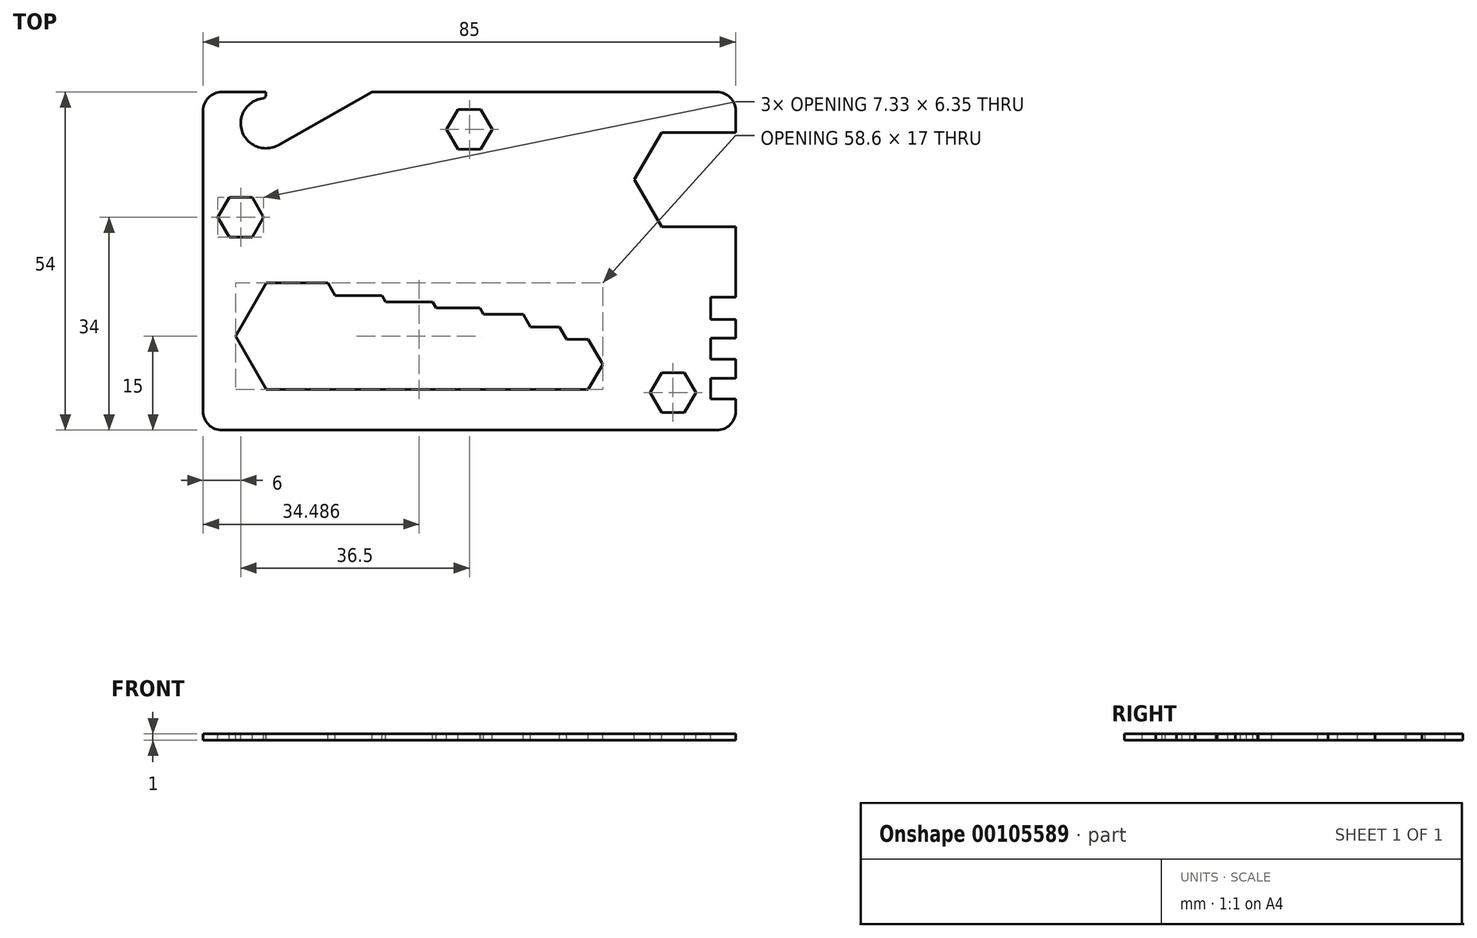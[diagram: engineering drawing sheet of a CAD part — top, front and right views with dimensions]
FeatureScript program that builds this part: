
annotation { "Feature Type Name" : "Feature", "Feature Type Description" : "" }
export const myFeature = defineFeature(function(context is Context, id is Id, definition is map)
    precondition{}
    {
        {
            var Q0;
            Q0=qCreatedBy(makeId("Top.planeOp"),FACE);
            var sketch = newSketch(context, id + "F0", { "sketchPlane" : qUnion([Q0])});
            skLineSegment(sketch, "E0.bottom", {"start": v(-42.5, 27) * mm, "end": v(42.5, 27) * mm});
            skLineSegment(sketch, "E0.top", {"start": v(-42.5, -27) * mm, "end": v(42.5, -27) * mm});
            skLineSegment(sketch, "E0.left", {"start": v(-42.5, 27) * mm, "end": v(-42.5, -27) * mm});
            skLineSegment(sketch, "E0.right", {"start": v(42.5, 27) * mm, "end": v(42.5, -27) * mm});
            skPoint(sketch, "E0.middle", {"position": v(0, 0) * mm});
            skSolve(sketch);
        }
        {
            var Q0;
            Q0 = qSketchRegion(id + "F0", true);
            extrude(context, id + "F1", {"entities" : qUnion([Q0]), "depth" : 1 * mm});
        }
        {
            var Q0;
            Q0=makeQuery(id+"F1.opExtrude","SWEPT_EDGE",EDGE,{"disambiguationData":[OSD([sQuery(id+"F0.wireOp",EDGE,"E0.top"),sQuery(id+"F0.wireOp",EDGE,"E0.left")])]});
            var Q1;
            Q1=makeQuery(id+"F1.opExtrude","SWEPT_EDGE",EDGE,{"disambiguationData":[OSD([sQuery(id+"F0.wireOp",EDGE,"E0.bottom"),sQuery(id+"F0.wireOp",EDGE,"E0.left")])]});
            var Q2;
            Q2=makeQuery(id+"F1.opExtrude","SWEPT_EDGE",EDGE,{"disambiguationData":[OSD([sQuery(id+"F0.wireOp",EDGE,"E0.top"),sQuery(id+"F0.wireOp",EDGE,"E0.right")])]});
            var Q3;
            Q3=makeQuery(id+"F1.opExtrude","SWEPT_EDGE",EDGE,{"disambiguationData":[OSD([sQuery(id+"F0.wireOp",EDGE,"E0.bottom"),sQuery(id+"F0.wireOp",EDGE,"E0.right")])]});
            fillet(context, id + "F2", {"entities" : qUnion([Q0, Q1, Q2, Q3]), "radius" : 3 * mm, "tangentPropagation" : true, "allowEdgeOverflow" : false});
        }
        {
            var Q0;
            Q0=makeQuery(id+"F1.opExtrude","CAP_FACE",FACE,{"disambiguationData":[OSD([sQuery(id+"F0.wireOp",EDGE,"E0.bottom"),sQuery(id+"F0.wireOp",EDGE,"E0.top"),sQuery(id+"F0.wireOp",EDGE,"E0.left"),sQuery(id+"F0.wireOp",EDGE,"E0.right")])],"isStart":false});
            var sketch = newSketch(context, id + "F3", { "sketchPlane" : qUnion([Q0])});
            skCircle(sketch, "E1.cCircle", {"center": v(-27.5, -12) * mm, "radius": 8.5 * mm, "construction": true});
            skLineSegment(sketch, "E1.0", {"start": v(-32.4, -3.5) * mm, "end": v(-22.6, -3.5) * mm});
            skLineSegment(sketch, "E1.1", {"start": v(-22.6, -3.5) * mm, "end": v(-21.44, -5.5) * mm});
            skLineSegment(sketch, "E1.3", {"start": v(-22.6, -20.5) * mm, "end": v(-32.4, -20.5) * mm});
            skLineSegment(sketch, "E1.4", {"start": v(-32.4, -20.5) * mm, "end": v(-37.31, -12) * mm});
            skLineSegment(sketch, "E1.5", {"start": v(-37.31, -12) * mm, "end": v(-32.4, -3.5) * mm});
            skPoint(sketch, "E1.0.midPoint", {"position": v(-27.5, -3.5) * mm});
            skCircle(sketch, "E2.cCircle", {"center": v(-18.26, -13) * mm, "radius": 7.5 * mm, "construction": true});
            skLineSegment(sketch, "E2.1", {"start": v(-13.93, -5.5) * mm, "end": v(-13.35, -6.5) * mm});
            skLineSegment(sketch, "E2.3", {"start": v(-13.93, -20.5) * mm, "end": v(-22.6, -20.5) * mm});
            skPoint(sketch, "E2.0.midPoint", {"position": v(-18.26, -5.5) * mm});
            skCircle(sketch, "E3.cCircle", {"center": v(-9.9, -13.5) * mm, "radius": 7 * mm, "construction": true});
            skLineSegment(sketch, "E3.0", {"start": v(-13.35, -6.5) * mm, "end": v(-5.85, -6.5) * mm});
            skLineSegment(sketch, "E3.1", {"start": v(-5.85, -6.5) * mm, "end": v(-5.27, -7.5) * mm});
            skLineSegment(sketch, "E3.3", {"start": v(-5.85, -20.5) * mm, "end": v(-13.93, -20.5) * mm});
            skPoint(sketch, "E3.0.midPoint", {"position": v(-9.9, -6.5) * mm});
            skCircle(sketch, "E4.cCircle", {"center": v(-2.1, -14) * mm, "radius": 6.5 * mm, "construction": true});
            skLineSegment(sketch, "E4.0", {"start": v(-5.27, -7.5) * mm, "end": v(1.66, -7.5) * mm});
            skLineSegment(sketch, "E4.1", {"start": v(1.66, -7.5) * mm, "end": v(2.23, -8.5) * mm});
            skLineSegment(sketch, "E4.3", {"start": v(1.66, -20.5) * mm, "end": v(-5.85, -20.5) * mm});
            skPoint(sketch, "E4.0.midPoint", {"position": v(-2.1, -7.5) * mm});
            skCircle(sketch, "E5.cCircle", {"center": v(5.12, -14.5) * mm, "radius": 6 * mm, "construction": true});
            skLineSegment(sketch, "E5.0", {"start": v(2.23, -8.5) * mm, "end": v(8.58, -8.5) * mm});
            skLineSegment(sketch, "E5.1", {"start": v(8.58, -8.5) * mm, "end": v(9.74, -10.5) * mm});
            skLineSegment(sketch, "E5.3", {"start": v(8.58, -20.5) * mm, "end": v(1.66, -20.5) * mm});
            skPoint(sketch, "E5.0.midPoint", {"position": v(5.12, -8.5) * mm});
            skCircle(sketch, "E6.cCircle", {"center": v(11.47, -15.5) * mm, "radius": 5 * mm, "construction": true});
            skLineSegment(sketch, "E6.0", {"start": v(9.74, -10.5) * mm, "end": v(14.36, -10.5) * mm});
            skLineSegment(sketch, "E6.1", {"start": v(14.36, -10.5) * mm, "end": v(15.51, -12.5) * mm});
            skLineSegment(sketch, "E6.3", {"start": v(14.36, -20.5) * mm, "end": v(8.58, -20.5) * mm});
            skPoint(sketch, "E6.0.midPoint", {"position": v(11.47, -10.5) * mm});
            skCircle(sketch, "E7.cCircle", {"center": v(16.67, -16.5) * mm, "radius": 4 * mm, "construction": true});
            skLineSegment(sketch, "E7.0", {"start": v(15.51, -12.5) * mm, "end": v(18.98, -12.5) * mm});
            skLineSegment(sketch, "E7.1", {"start": v(18.98, -12.5) * mm, "end": v(21.29, -16.5) * mm});
            skLineSegment(sketch, "E7.2", {"start": v(21.29, -16.5) * mm, "end": v(18.98, -20.5) * mm});
            skLineSegment(sketch, "E7.3", {"start": v(18.98, -20.5) * mm, "end": v(14.36, -20.5) * mm});
            skPoint(sketch, "E7.0.midPoint", {"position": v(16.67, -12.5) * mm});
            skPoint(sketch, "E8.orphan", {"position": v(14.36, -12.5) * mm});
            skPoint(sketch, "E9.orphan", {"position": v(8.58, -10.5) * mm});
            skPoint(sketch, "E10.orphan", {"position": v(5.4, -14) * mm});
            skPoint(sketch, "E11.orphan", {"position": v(-1.8, -13.5) * mm});
            skPoint(sketch, "E12.trimOffspring.end.orphan", {"position": v(-5.85, -7.5) * mm});
            skPoint(sketch, "E13.trimOffspring.end.orphan", {"position": v(1.66, -8.5) * mm});
            skPoint(sketch, "E14.orphan", {"position": v(-13.93, -6.5) * mm});
            skPoint(sketch, "E15.orphan", {"position": v(-9.6, -13) * mm});
            skPoint(sketch, "E16.orphan", {"position": v(-17.69, -12) * mm});
            skLineSegment(sketch, "E17.trimOffspring", {"start": v(-21.44, -5.5) * mm, "end": v(-13.93, -5.5) * mm});
            skPoint(sketch, "E2.5.end.orphan", {"position": v(-22.6, -5.5) * mm});
            skLineSegment(sketch, "E18", {"start": v(-22.6, -5.5) * mm, "end": v(-21.44, -5.5) * mm, "construction": true});
            skLineSegment(sketch, "E19", {"start": v(-22.6, -20.5) * mm, "end": v(-18.26, -13) * mm, "construction": true});
            skLineSegment(sketch, "E20", {"start": v(-18.26, -13) * mm, "end": v(-17.69, -12) * mm, "construction": true});
            skLineSegment(sketch, "E21", {"start": v(-17.69, -12) * mm, "end": v(-21.44, -5.5) * mm, "construction": true});
            skLineSegment(sketch, "E22", {"start": v(-13.35, -6.5) * mm, "end": v(-9.6, -13) * mm, "construction": true});
            skLineSegment(sketch, "E23", {"start": v(-9.6, -13) * mm, "end": v(-9.9, -13.5) * mm, "construction": true});
            skLineSegment(sketch, "E24", {"start": v(-9.9, -13.5) * mm, "end": v(-13.93, -20.5) * mm, "construction": true});
            skLineSegment(sketch, "E25", {"start": v(-13.35, -6.5) * mm, "end": v(-13.93, -6.5) * mm, "construction": true});
            skLineSegment(sketch, "E26", {"start": v(-5.27, -7.5) * mm, "end": v(-1.8, -13.5) * mm, "construction": true});
            skLineSegment(sketch, "E27", {"start": v(-2.1, -14) * mm, "end": v(-1.8, -13.5) * mm, "construction": true});
            skLineSegment(sketch, "E28", {"start": v(-2.1, -14) * mm, "end": v(-5.85, -20.5) * mm, "construction": true});
            skSolve(sketch);
        }
        {
            var Q0;
            Q0 = qSketchRegion(id + "F3", true);
            extrude(context, id + "F4", {"entities" : qUnion([Q0]), "operationType" : NewBodyOperationType.REMOVE, "endBound" : BoundingType.THROUGH_ALL, "oppositeDirection" : true, "depth" : 25 * mm});
        }
        {
            var Q0;
            Q0=makeQuery(id+"F1.opExtrude","CAP_FACE",FACE,{"disambiguationData":[OSD([sQuery(id+"F0.wireOp",EDGE,"E0.bottom"),sQuery(id+"F0.wireOp",EDGE,"E0.top"),sQuery(id+"F0.wireOp",EDGE,"E0.left"),sQuery(id+"F0.wireOp",EDGE,"E0.right")])],"isStart":false});
            var sketch = newSketch(context, id + "F5", { "sketchPlane" : qUnion([Q0])});
            skLineSegment(sketch, "E29.bottom", {"start": v(42.5, -5.75) * mm, "end": v(38.5, -5.75) * mm});
            skLineSegment(sketch, "E29.top", {"start": v(42.5, -9.3) * mm, "end": v(38.5, -9.3) * mm});
            skLineSegment(sketch, "E29.left", {"start": v(42.5, -5.75) * mm, "end": v(42.5, -9.3) * mm});
            skLineSegment(sketch, "E29.right", {"start": v(38.5, -5.75) * mm, "end": v(38.5, -9.3) * mm});
            skLineSegment(sketch, "E30.bottom", {"start": v(42.5, -12.3) * mm, "end": v(38.5, -12.3) * mm});
            skLineSegment(sketch, "E30.top", {"start": v(42.5, -15.7) * mm, "end": v(38.5, -15.7) * mm});
            skLineSegment(sketch, "E30.left", {"start": v(42.5, -12.3) * mm, "end": v(42.5, -15.7) * mm});
            skLineSegment(sketch, "E30.right", {"start": v(38.5, -12.3) * mm, "end": v(38.5, -15.7) * mm});
            skLineSegment(sketch, "E31.bottom", {"start": v(42.5, -18.7) * mm, "end": v(38.5, -18.7) * mm});
            skLineSegment(sketch, "E31.top", {"start": v(42.5, -22) * mm, "end": v(38.5, -22) * mm});
            skLineSegment(sketch, "E31.left", {"start": v(42.5, -18.7) * mm, "end": v(42.5, -22) * mm});
            skLineSegment(sketch, "E31.right", {"start": v(38.5, -18.7) * mm, "end": v(38.5, -22) * mm});
            skSolve(sketch);
        }
        {
            var Q0;
            Q0 = qSketchRegion(id + "F5", true);
            extrude(context, id + "F6", {"entities" : qUnion([Q0]), "operationType" : NewBodyOperationType.REMOVE, "endBound" : BoundingType.THROUGH_ALL, "oppositeDirection" : true, "depth" : 25 * mm});
        }
        {
            var Q0;
            Q0=makeQuery(id+"F1.opExtrude","CAP_FACE",FACE,{"disambiguationData":[OSD([sQuery(id+"F0.wireOp",EDGE,"E0.bottom"),sQuery(id+"F0.wireOp",EDGE,"E0.top"),sQuery(id+"F0.wireOp",EDGE,"E0.left"),sQuery(id+"F0.wireOp",EDGE,"E0.right")])],"isStart":false});
            var sketch = newSketch(context, id + "F7", { "sketchPlane" : qUnion([Q0])});
            skCircle(sketch, "E32.cCircle", {"center": v(35, 13) * mm, "radius": 7.5 * mm, "construction": true});
            skLineSegment(sketch, "E32.0", {"start": v(30.67, 20.5) * mm, "end": v(42.5, 20.5) * mm});
            skLineSegment(sketch, "E32.3", {"start": v(42.5, 5.5) * mm, "end": v(30.67, 5.5) * mm});
            skLineSegment(sketch, "E32.4", {"start": v(30.67, 5.5) * mm, "end": v(26.34, 13) * mm});
            skLineSegment(sketch, "E32.5", {"start": v(26.34, 13) * mm, "end": v(30.67, 20.5) * mm});
            skPoint(sketch, "E32.0.midPoint", {"position": v(35, 20.5) * mm});
            skLineSegment(sketch, "E33", {"start": v(42.5, 20.5) * mm, "end": v(42.5, 5.5) * mm});
            skSolve(sketch);
        }
        {
            var Q0;
            Q0 = qSketchRegion(id + "F7", true);
            extrude(context, id + "F8", {"entities" : qUnion([Q0]), "operationType" : NewBodyOperationType.REMOVE, "endBound" : BoundingType.THROUGH_ALL, "oppositeDirection" : true, "depth" : 25 * mm});
        }
        {
            var Q0;
            Q0=makeQuery(id+"F1.opExtrude","CAP_FACE",FACE,{"disambiguationData":[OSD([sQuery(id+"F0.wireOp",EDGE,"E0.bottom"),sQuery(id+"F0.wireOp",EDGE,"E0.top"),sQuery(id+"F0.wireOp",EDGE,"E0.left"),sQuery(id+"F0.wireOp",EDGE,"E0.right")])],"isStart":false});
            var sketch = newSketch(context, id + "F9", { "sketchPlane" : qUnion([Q0])});
            skArc(sketch, "E34", {"start": v(-32.5, 26) * mm, "mid": v(-36.37, 20.98) * mm, "end": v(-30.53, 18.52) * mm});
            skLineSegment(sketch, "E35", {"start": v(-30.53, 18.52) * mm, "end": v(-15.5, 27) * mm});
            skLineSegment(sketch, "E36", {"start": v(-32.5, 27) * mm, "end": v(-32.5, 26) * mm});
            skLineSegment(sketch, "E37", {"start": v(-32.5, 27) * mm, "end": v(-15.5, 27) * mm});
            skSolve(sketch);
        }
        {
            var Q0;
            Q0 = qSketchRegion(id + "F9", true);
            extrude(context, id + "F10", {"entities" : qUnion([Q0]), "operationType" : NewBodyOperationType.REMOVE, "endBound" : BoundingType.THROUGH_ALL, "oppositeDirection" : true, "depth" : 25 * mm});
        }
        {
            var Q0;
            Q0=makeQuery(id+"F10.boolean.opBoolean","COPY",EDGE,{"derivedFrom":makeQuery(id+"F10.opExtrude","SWEPT_EDGE",EDGE,{"disambiguationData":[OSD([sQuery(id+"F9.wireOp",EDGE,"E34"),sQuery(id+"F9.wireOp",EDGE,"E36")])]})});
            var Q1;
            Q1=makeQuery(id+"F10.boolean.opBoolean","COPY",EDGE,{"derivedFrom":makeQuery(id+"F10.opExtrude","SWEPT_EDGE",EDGE,{"disambiguationData":[OSD([sQuery(id+"F0.wireOp",EDGE,"E0.bottom"),sQuery(id+"F9.wireOp",EDGE,"E36"),sQuery(id+"F9.wireOp",EDGE,"E37")])]})});
            fillet(context, id + "F11", {"entities" : qUnion([Q0, Q1]), "radius" : .5 * mm, "tangentPropagation" : true, "allowEdgeOverflow" : false});
        }
        {
            var Q0;
            Q0=makeQuery(id+"F1.opExtrude","CAP_FACE",FACE,{"disambiguationData":[OSD([sQuery(id+"F0.wireOp",EDGE,"E0.bottom"),sQuery(id+"F0.wireOp",EDGE,"E0.top"),sQuery(id+"F0.wireOp",EDGE,"E0.left"),sQuery(id+"F0.wireOp",EDGE,"E0.right")])],"isStart":false});
            var sketch = newSketch(context, id + "F12", { "sketchPlane" : qUnion([Q0])});
            skCircle(sketch, "E38.cCircle", {"center": v(0, 21) * mm, "radius": 3.17 * mm, "construction": true});
            skLineSegment(sketch, "E38.0", {"start": v(-1.83, 24.17) * mm, "end": v(1.83, 24.17) * mm});
            skLineSegment(sketch, "E38.1", {"start": v(1.83, 24.17) * mm, "end": v(3.67, 21) * mm});
            skLineSegment(sketch, "E38.2", {"start": v(3.67, 21) * mm, "end": v(1.83, 17.82) * mm});
            skLineSegment(sketch, "E38.3", {"start": v(1.83, 17.82) * mm, "end": v(-1.83, 17.82) * mm});
            skLineSegment(sketch, "E38.4", {"start": v(-1.83, 17.82) * mm, "end": v(-3.67, 21) * mm});
            skLineSegment(sketch, "E38.5", {"start": v(-3.67, 21) * mm, "end": v(-1.83, 24.17) * mm});
            skPoint(sketch, "E38.0.midPoint", {"position": v(0, 24.17) * mm});
            skCircle(sketch, "E39.cCircle", {"center": v(32.5, -21) * mm, "radius": 3.17 * mm, "construction": true});
            skLineSegment(sketch, "E39.0", {"start": v(30.67, -17.82) * mm, "end": v(34.33, -17.82) * mm});
            skLineSegment(sketch, "E39.1", {"start": v(34.33, -17.82) * mm, "end": v(36.17, -21) * mm});
            skLineSegment(sketch, "E39.2", {"start": v(36.17, -21) * mm, "end": v(34.33, -24.17) * mm});
            skLineSegment(sketch, "E39.3", {"start": v(34.33, -24.17) * mm, "end": v(30.67, -24.17) * mm});
            skLineSegment(sketch, "E39.4", {"start": v(30.67, -24.17) * mm, "end": v(28.83, -21) * mm});
            skLineSegment(sketch, "E39.5", {"start": v(28.83, -21) * mm, "end": v(30.67, -17.82) * mm});
            skPoint(sketch, "E39.0.midPoint", {"position": v(32.5, -17.82) * mm});
            skCircle(sketch, "E40.cCircle", {"center": v(-36.5, 7) * mm, "radius": 3.17 * mm, "construction": true});
            skLineSegment(sketch, "E40.0", {"start": v(-38.33, 10.17) * mm, "end": v(-34.67, 10.17) * mm});
            skLineSegment(sketch, "E40.1", {"start": v(-34.67, 10.17) * mm, "end": v(-32.83, 7) * mm});
            skLineSegment(sketch, "E40.2", {"start": v(-32.83, 7) * mm, "end": v(-34.67, 3.82) * mm});
            skLineSegment(sketch, "E40.3", {"start": v(-34.67, 3.82) * mm, "end": v(-38.33, 3.82) * mm});
            skLineSegment(sketch, "E40.4", {"start": v(-38.33, 3.82) * mm, "end": v(-40.17, 7) * mm});
            skLineSegment(sketch, "E40.5", {"start": v(-40.17, 7) * mm, "end": v(-38.33, 10.17) * mm});
            skPoint(sketch, "E40.0.midPoint", {"position": v(-36.5, 10.17) * mm});
            skSolve(sketch);
        }
        {
            var Q0;
            Q0 = qSketchRegion(id + "F12", true);
            extrude(context, id + "F13", {"entities" : qUnion([Q0]), "operationType" : NewBodyOperationType.REMOVE, "endBound" : BoundingType.THROUGH_ALL, "oppositeDirection" : true, "depth" : 25 * mm});
        }
    });
